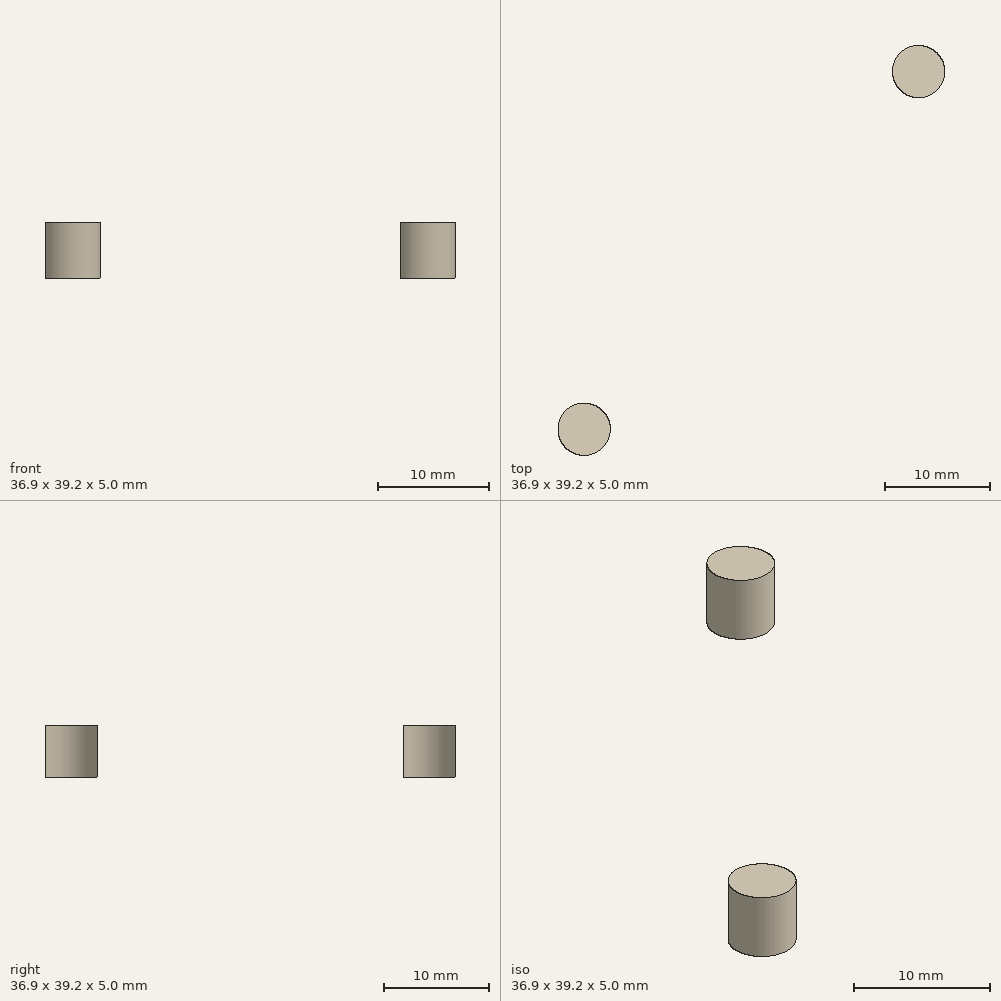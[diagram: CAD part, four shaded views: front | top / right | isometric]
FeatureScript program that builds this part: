
annotation { "Feature Type Name" : "Feature", "Feature Type Description" : "" }
export const myFeature = defineFeature(function(context is Context, id is Id, definition is map)
    precondition{}
    {
        {
            var Q0;
            Q0=qCreatedBy(makeId("Top.planeOp"),FACE);
            var sketch = newSketch(context, id + "F0", { "sketchPlane" : qUnion([Q0])});
            skCircle(sketch, "E0", {"center": v(0, 0) * mm, "radius": 42.5 * mm});
            skCircle(sketch, "E1", {"center": v(0, 0) * mm, "radius": 37.5 * mm});
            skSolve(sketch);
        }
        {
            var Q0;
            Q0=makeQuery(id+"F0.imprint","IMPRINT",FACE,{"disambiguationData":[TD([[makeQuery(id+"F0.imprint","IMPRINT",EDGE,{"derivedFrom":sQuery(id+"F0.wireOp",EDGE,"E1")}),1.0]])]});
            extrude(context, id + "F1", {"entities" : qUnion([Q0]), "oppositeDirection" : true, "depth" : 3 * mm});
        }
        {
            var Q0;
            Q0=makeQuery(id+"F0.imprint","IMPRINT",FACE,{"disambiguationData":[TD([[makeQuery(id+"F0.imprint","IMPRINT",EDGE,{"derivedFrom":sQuery(id+"F0.wireOp",EDGE,"E0")}),1.0]])]});
            var Q1;
            Q1=makeQuery(id+"F0.imprint","IMPRINT",FACE,{"disambiguationData":[TD([[makeQuery(id+"F0.imprint","IMPRINT",EDGE,{"derivedFrom":sQuery(id+"F0.wireOp",EDGE,"E1")}),1.0]])]});
            extrude(context, id + "F2", {"entities" : qUnion([Q0, Q1]), "operationType" : NewBodyOperationType.ADD, "depth" : 2 * mm});
        }
        {
            var Q0;
            Q0=makeQuery(id+"F2.opExtrude","CAP_FACE",FACE,{"disambiguationData":[OSD([sQuery(id+"F0.wireOp",EDGE,"E0")])],"isStart":false});
            var sketch = newSketch(context, id + "F3", { "sketchPlane" : qUnion([Q0])});
            skLineSegment(sketch, "E2", {"start": v(0, 42.5) * mm, "end": v(0, -42.5) * mm, "construction": true});
            skLineSegment(sketch, "E3", {"start": v(-42.5, 0) * mm, "end": v(42.5, 0) * mm, "construction": true});
            skCircle(sketch, "E4", {"center": v(-15.97, 17.08) * mm, "radius": 2.5 * mm});
            skCircle(sketch, "E5.MirrorC", {"center": v(-15.97, -17.08) * mm, "radius": 2.5 * mm});
            skLineSegment(sketch, "E6.MirrorCS", {"start": v(0, -42.5) * mm, "end": v(0, 42.5) * mm, "construction": true});
            skCircle(sketch, "E7.MirrorC", {"center": v(15.97, 17.08) * mm, "radius": 2.5 * mm});
            skCircle(sketch, "E8.MirrorC", {"center": v(15.97, -17.08) * mm, "radius": 2.5 * mm});
            skSolve(sketch);
        }
        {
            var Q0;
            Q0=makeQuery(id+"F3.imprint","IMPRINT",FACE,{"disambiguationData":[TD([[makeQuery(id+"F3.imprint","IMPRINT",EDGE,{"derivedFrom":sQuery(id+"F3.wireOp",EDGE,"E7.MirrorC")}),-1.0]])]});
            var Q1;
            Q1=makeQuery(id+"F3.imprint","IMPRINT",FACE,{"disambiguationData":[TD([[makeQuery(id+"F3.imprint","IMPRINT",EDGE,{"derivedFrom":sQuery(id+"F3.wireOp",EDGE,"E8.MirrorC")}),1.0]])]});
            var Q2;
            Q2=makeQuery(id+"F3.imprint","IMPRINT",FACE,{"disambiguationData":[TD([[makeQuery(id+"F3.imprint","IMPRINT",EDGE,{"derivedFrom":sQuery(id+"F3.wireOp",EDGE,"E5.MirrorC")}),-1.0]])]});
            var Q3;
            Q3=makeQuery(id+"F3.imprint","IMPRINT",FACE,{"disambiguationData":[TD([[makeQuery(id+"F3.imprint","IMPRINT",EDGE,{"derivedFrom":sQuery(id+"F3.wireOp",EDGE,"E4")}),1.0]])]});
            extrude(context, id + "F4", {"entities" : qUnion([Q0, Q1, Q2, Q3]), "operationType" : NewBodyOperationType.REMOVE, "oppositeDirection" : true, "depth" : 25 * mm});
        }
    });
